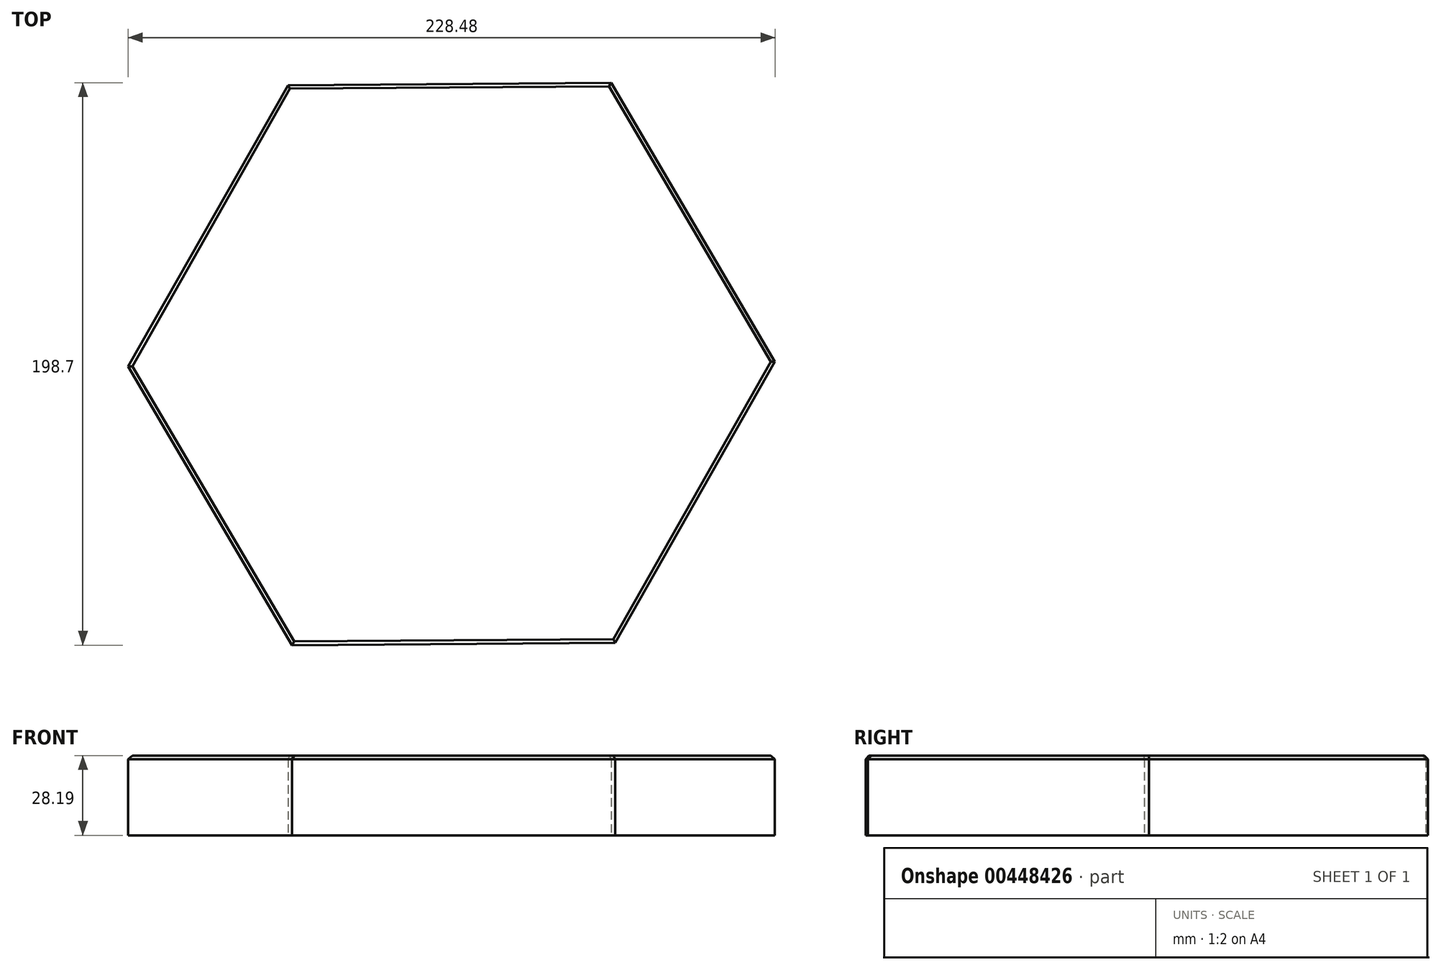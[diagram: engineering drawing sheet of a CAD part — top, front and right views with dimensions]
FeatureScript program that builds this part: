
annotation { "Feature Type Name" : "Feature", "Feature Type Description" : "" }
export const myFeature = defineFeature(function(context is Context, id is Id, definition is map)
    precondition{}
    {
        {
            var Q0;
            Q0=qCreatedBy(makeId("Top.planeOp"),FACE);
            var sketch = newSketch(context, id + "F0", { "sketchPlane" : qUnion([Q0])});
            skCircle(sketch, "E0.cCircle", {"center": v(-0.48, 0.86) * mm, "radius": 98.94 * mm, "construction": true});
            skLineSegment(sketch, "E0.0", {"start": v(-114.72, 0.03) * mm, "end": v(-58.32, 99.38) * mm});
            skLineSegment(sketch, "E0.1", {"start": v(-58.32, 99.38) * mm, "end": v(55.92, 100.2) * mm});
            skLineSegment(sketch, "E0.2", {"start": v(55.92, 100.2) * mm, "end": v(113.76, 1.69) * mm});
            skLineSegment(sketch, "E0.3", {"start": v(113.76, 1.69) * mm, "end": v(57.35, -97.66) * mm});
            skLineSegment(sketch, "E0.4", {"start": v(57.35, -97.66) * mm, "end": v(-56.89, -98.49) * mm});
            skLineSegment(sketch, "E0.5", {"start": v(-56.89, -98.49) * mm, "end": v(-114.72, 0.03) * mm});
            skPoint(sketch, "E0.0.midPoint", {"position": v(-86.52, 49.7) * mm});
            skSolve(sketch);
        }
        {
            var Q0;
            Q0=makeQuery(id+"F0.imprint","IMPRINT",FACE,{"disambiguationData":[TD([[makeQuery(id+"F0.imprint","IMPRINT",EDGE,{"derivedFrom":sQuery(id+"F0.wireOp",EDGE,"E0.0")}),-1.0]])]});
            extrude(context, id + "F1", {"entities" : qUnion([Q0]), "depth" : 28.2 * mm});
        }
        {
            var Q0;
            Q0=makeQuery(id+"F1.opExtrude","CAP_FACE",FACE,{"disambiguationData":[OSD([sQuery(id+"F0.wireOp",EDGE,"E0.0"),sQuery(id+"F0.wireOp",EDGE,"E0.1"),sQuery(id+"F0.wireOp",EDGE,"E0.2"),sQuery(id+"F0.wireOp",EDGE,"E0.3"),sQuery(id+"F0.wireOp",EDGE,"E0.4"),sQuery(id+"F0.wireOp",EDGE,"E0.5")])],"isStart":false});
            chamfer(context, id + "F2", {"entities" : qUnion([Q0]), "width" : 1.27 * mm, "tangentPropagation" : true});
        }
    });
